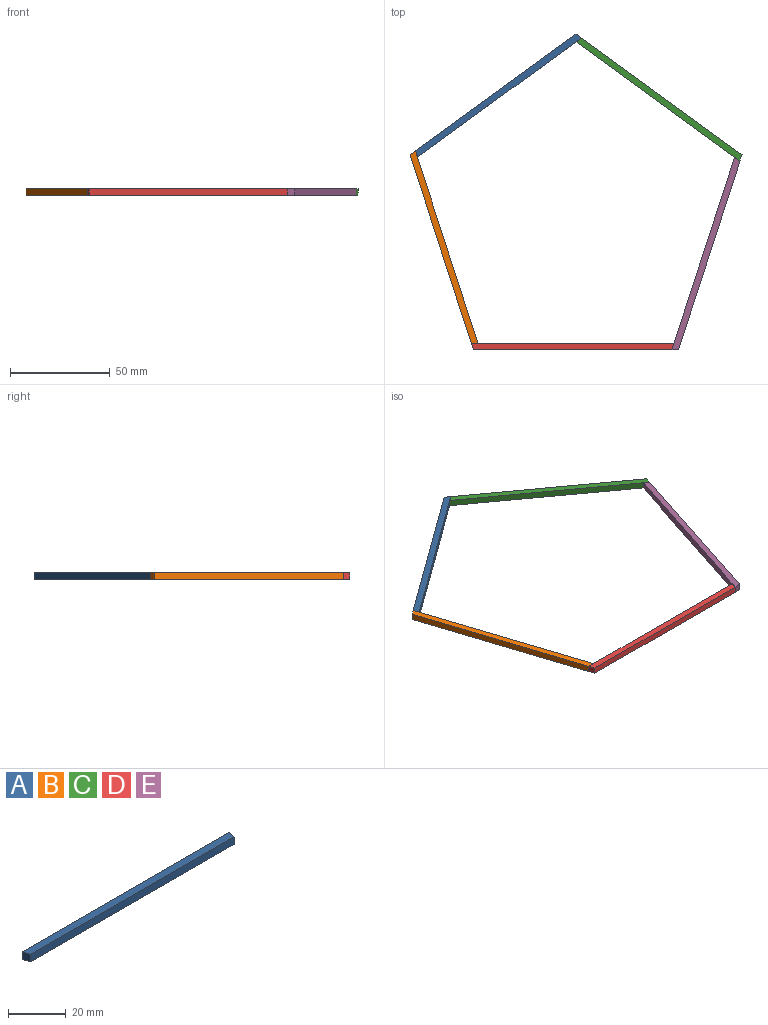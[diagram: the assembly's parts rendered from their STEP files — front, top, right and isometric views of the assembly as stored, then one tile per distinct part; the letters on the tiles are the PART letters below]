
ASSEMBLY  parts=5 mates=13
PART A: 6 faces, bbox 101.6x3.2x3.2 mm
  f0: plane 101.6x3.18mm, normal (0,0,1), area 319.3mm2, adj f2,f3,f4,f5
  f1: plane 101.6x3.18mm, normal (0,0,-1), area 319.3mm2, adj f2,f3,f4,f5
  f2: plane 99.54x3.18mm, normal (0,-1,0), area 316mm2, adj f0,f1,f4,f5
  f3: plane 101.6x3.18mm, normal (0,1,0), area 322.6mm2, adj f0,f1,f4,f5
  f4: plane 3.18x3.18mm, normal (-0.95,-0.31,0), area 10.6mm2, adj f0,f1,f2,f3
  f5: plane 3.18x3.18mm, normal (0.95,-0.31,0), area 10.6mm2, adj f0,f1,f2,f3
PART B: same geometry as A
PART C: same geometry as A
PART D: same geometry as A
PART E: same geometry as A
PLACE A rot(axis=(0,0,-1),144deg) t=(-25.25,107.15,33.24)mm
PLACE B rot(axis=(-0.59,-0.81,0),180deg) t=(-32.56,91.02,25.14)mm
PLACE C rot(axis=(0,0,1),144deg) t=(54.24,150.16,33.24)mm
PLACE D t=(80.68,6.33,33.24)mm
PLACE E rot(axis=(0,0,1),72deg) t=(119.71,87.85,33.24)mm
MATE parallel A.f0 <-> D.f0  axis (0,0,1) through (4.77,130.92,30.78)mm
MATE planar A.f5 <-> B.f3  axis (-0.95,-0.31,0) through (-35.92,101.37,29.19)mm
MATE planar C.f1 <-> E.f1  axis (0,0,-1) through (86.12,128.96,27.6)mm
MATE planar B.f5 <-> A.f2  axis (-0.59,0.81,0) through (-37.78,101.97,29.19)mm
MATE planar E.f5 <-> C.f3  axis (0.59,0.81,0) through (124.94,98.8,29.19)mm
MATE planar C.f5 <-> A.f3  axis (-0.59,0.81,0) through (45.44,158.52,29.19)mm
MATE planar B.f4 <-> D.f3  axis (0,-1,0) through (-6.71,6.33,29.19)mm
MATE parallel B.f4 <-> D.f3  axis (0,-1,0) through (-6.71,6.33,29.19)mm
MATE planar B.f0 <-> A.f1  axis (0,0,-1) through (-22.24,54.15,27.6)mm
MATE planar B.f0 <-> D.f1  axis (0,0,-1) through (-22.24,54.15,27.6)mm
MATE planar C.f2 <-> A.f4  axis (0.59,0.81,0) through (87.06,130.24,29.19)mm
MATE planar E.f2 <-> C.f4  axis (0.95,-0.31,0) through (110.91,50.48,29.19)mm
MATE planar B.f2 <-> D.f4  axis (-0.95,-0.31,0) through (-23.76,53.66,29.19)mm
